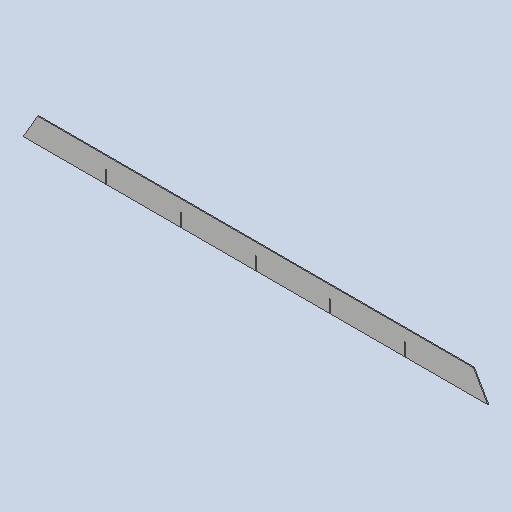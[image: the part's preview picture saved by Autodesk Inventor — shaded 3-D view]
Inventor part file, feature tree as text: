
AUTODESK INVENTOR PART (.ipt)
format: ipt  version: 2025 (Build 290162010, 162A)  size: 323,584 bytes
history: native  units: mm
features: sketch x2, other x2, sheet_metal_op x1, extrude x1, pattern_linear x1
ambient origin geometry x8: Origin, YZ Plane, XZ Plane, XY Plane, X Axis, Y Axis, Z Axis, Center Point
bodies: Solid1 (feature_tree)
feature tree (7):
  sheet_metal_op  "Face1"
  extrude  "Extrusion1"  Depth=80.0mm
  pattern_linear  "Rectangular Pattern1"  Spacing1=120.0deg  [1 undecoded]
  sketch  "Sketch1"  dims[d0=80.0mm d1=1800.0mm]
  other  "Plate1"
  sketch  "Sketch2"  dims[d2=3.0mm d3=120.0deg d6=700.0mm d7=120.0deg d8=700.0mm d9=3.2mm d10=41.0mm d11=0.0mm d12=0.0mm d13=50.0mm d15=240.0mm]
  other  "Definition1"
note: 1 required parameter value undecoded (feature->parameter linkage not recoverable at this tier; creation-order binding heuristic only, values carry confidence <= 0.55)
